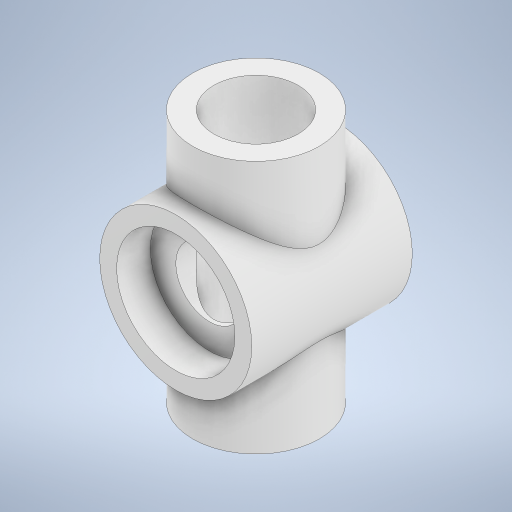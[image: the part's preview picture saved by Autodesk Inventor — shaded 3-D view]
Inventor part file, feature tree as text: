
AUTODESK INVENTOR PART (.ipt)
format: ipt  version: 2023 (Build 270158030, 158C)  size: 324,608 bytes
history: native  units: in
note: dims shown in document units (in); Inventor stores cm internally (conversion verified against a paired STEP export)
features: sketch x5, extrude x3, plane x1, revolve x1, mirror x1, hole x1
ambient origin geometry x8: Origin, YZ Plane, XZ Plane, XY Plane, X Axis, Y Axis, Z Axis, Center Point
bodies: Solid1 (feature_tree)
feature tree (12):
  extrude  "Extrusion1"  Depth=0.3937in
  plane  "Work Plane2"
  extrude  "Extrusion3"  Depth=0.5512in
  revolve  "Revolution1"  [1 undecoded]
  mirror  "Mirror3"
  extrude  "Extrusion4"  TaperAngle=360.0deg  [1 undecoded]
  hole  "Hole4"  [1 undecoded]
  sketch  "Sketch1"  dims[d3=1.1811in d4=0.0in d37=0.3937in]
  sketch  "Sketch7"  dims[d38=0.5906in d39=0.5512in]
  sketch  "Sketch8"  dims[d40=0.0787in d41=0.0591in d42=0.0in d43=0.0in d44=0.5512in]
  sketch  "Sketch9"  dims[d46=0.0787in d47=360.0deg]
  sketch  "Sketch10"  dims[d48=0.0in d49=0.0in d50=0.1575in d51=0.315in d52=0.2362in d53=0.1575in d54=0.0787in d55=90.0deg d56=0.315in d57=0.8108in]
note: 3 required parameter values undecoded (feature->parameter linkage not recoverable at this tier; creation-order binding heuristic only, values carry confidence <= 0.55)